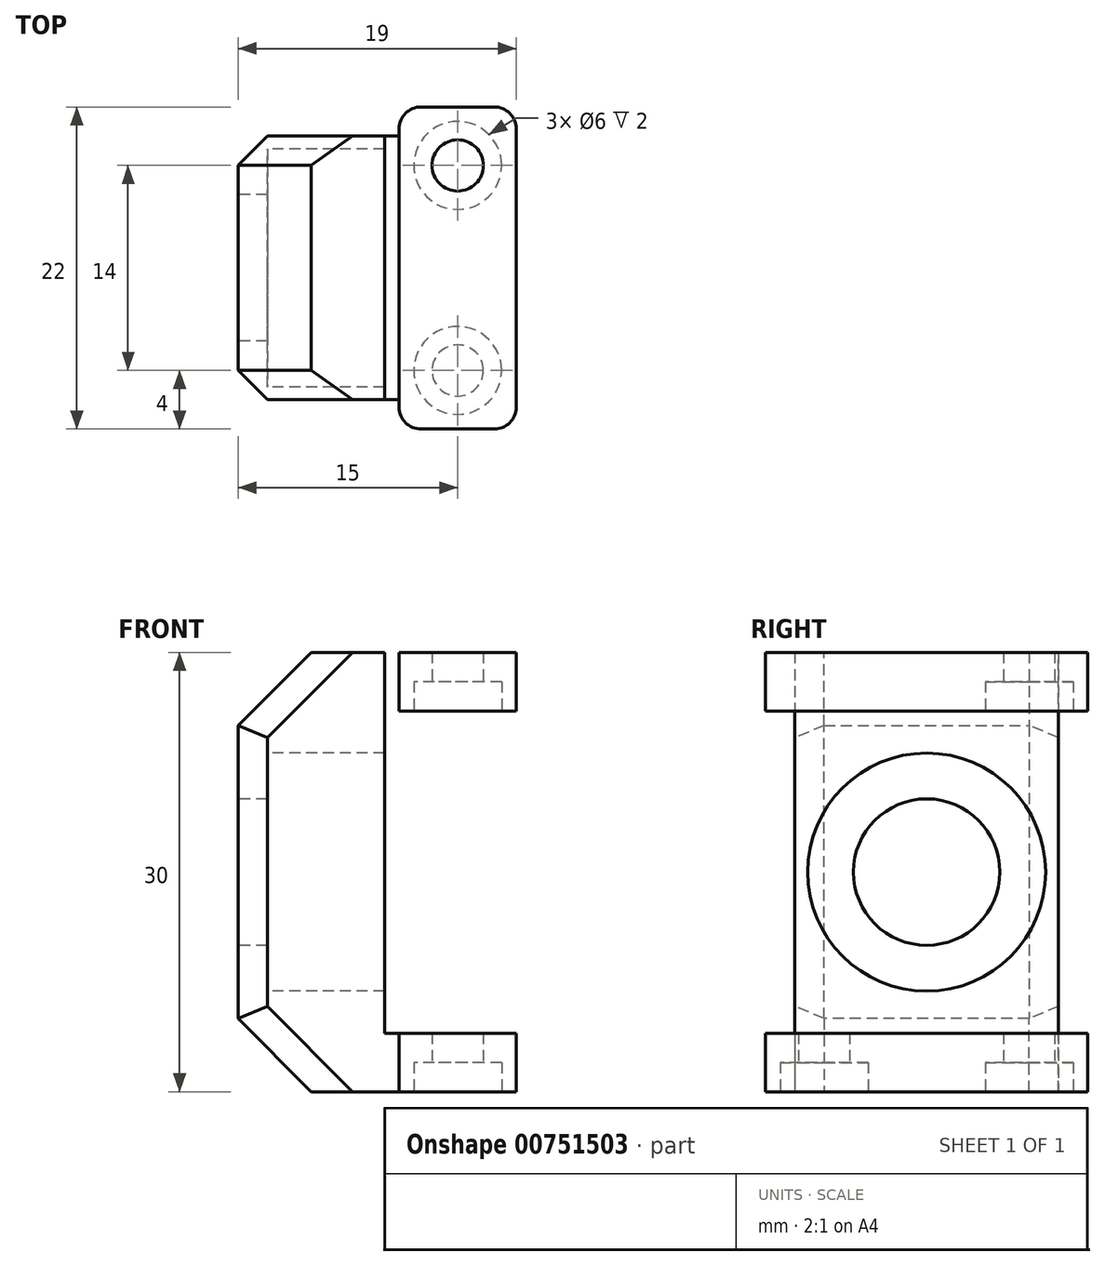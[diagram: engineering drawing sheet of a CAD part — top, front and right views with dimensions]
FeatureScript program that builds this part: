
annotation { "Feature Type Name" : "Feature", "Feature Type Description" : "" }
export const myFeature = defineFeature(function(context is Context, id is Id, definition is map)
    precondition{}
    {
        {
            assignVariable(context, id + "F0", {"name" : "UpperLowerWidth", "anyValue" : 4});
        }
        {
            assignVariable(context, id + "F1", {"name" : "TotalHeight", "anyValue" : 30});
        }
        {
            var Q0;
            Q0=qCreatedBy(makeId("Top.planeOp"),FACE);
            var sketch = newSketch(context, id + "F2", { "sketchPlane" : qUnion([Q0])});
            skLineSegment(sketch, "E0.bottom", {"start": v(-4, 11) * mm, "end": v(4, 11) * mm});
            skLineSegment(sketch, "E0.top", {"start": v(-4, -11) * mm, "end": v(4, -11) * mm});
            skLineSegment(sketch, "E0.left", {"start": v(-4, 11) * mm, "end": v(-4, -11) * mm});
            skLineSegment(sketch, "E0.right", {"start": v(4, 11) * mm, "end": v(4, -11) * mm});
            skPoint(sketch, "E0.middle", {"position": v(0, 0) * mm});
            skCircle(sketch, "E1", {"center": v(0, 7) * mm, "radius": 1.75 * mm});
            skCircle(sketch, "E2", {"center": v(0, -7) * mm, "radius": 1.75 * mm});
            skLineSegment(sketch, "E3.bottom", {"start": v(-4, 9) * mm, "end": v(-15, 9) * mm});
            skLineSegment(sketch, "E3.top", {"start": v(-4, -9) * mm, "end": v(-15, -9) * mm});
            skLineSegment(sketch, "E3.left", {"start": v(-4, 9) * mm, "end": v(-4, -9) * mm});
            skLineSegment(sketch, "E3.right", {"start": v(-15, 9) * mm, "end": v(-15, -9) * mm});
            skLineSegment(sketch, "E4", {"start": v(-4, 9) * mm, "end": v(-4, 11) * mm, "construction": true});
            skLineSegment(sketch, "E5", {"start": v(-4, -9) * mm, "end": v(-4, -11) * mm, "construction": true});
            skLineSegment(sketch, "E6", {"start": v(-5, -9) * mm, "end": v(-5, 9) * mm});
            skCircle(sketch, "E7", {"center": v(0, 7) * mm, "radius": 3 * mm});
            skCircle(sketch, "E8", {"center": v(0, -7) * mm, "radius": 3 * mm});
            skSolve(sketch);
        }
        {
            var Q0;
            {var subQ3=sQuery(id+"F2.wireOp",EDGE,"E0.bottom");Q0=makeQuery(id+"F2.imprint","IMPRINT",FACE,{"disambiguationData":[TD([[makeQuery(id+"F2.imprint","IMPRINT",EDGE,{"derivedFrom":subQ3}),-1.0]])]});}
            var Q1;
            {var subQ1=sQuery(id+"F2.wireOp",EDGE,"E0.top");Q1=makeQuery(id+"F2.imprint","IMPRINT",FACE,{"disambiguationData":[TD([[makeQuery(id+"F2.imprint","IMPRINT",EDGE,{"derivedFrom":subQ1}),1.0]])]});}
            var Q2;
            Q2=makeQuery(id+"F2.imprint","IMPRINT",FACE,{"disambiguationData":[TD([[makeQuery(id+"F2.imprint","IMPRINT",EDGE,{"derivedFrom":sQuery(id+"F2.wireOp",EDGE,"kTuUN5Vh-sZAy-PONC-NSCL-Ygs5GUUw9hLd")}),-1.0]])]});
            var Q3;
            Q3=makeQuery(id+"F2.imprint","IMPRINT",FACE,{"disambiguationData":[TD([[makeQuery(id+"F2.imprint","IMPRINT",EDGE,{"derivedFrom":sQuery(id+"F2.wireOp",EDGE,"kTuUN5Vh-sZAy-PONC-NSCL-Ygs5GUUw9hLd")}),1.0]])]});
            var Q4;
            {var subQ4=sQuery(id+"F2.wireOp",EDGE,"y2zxEj2q-xixG-cvwC-23qs-c7dRdEuyMa0k.left");Q4=makeQuery(id+"F2.imprint","IMPRINT",FACE,{"disambiguationData":[TD([[makeQuery(id+"F2.imprint","IMPRINT",EDGE,{"derivedFrom":subQ4}),-1.0]])]});}
            var Q5;
            {var subQ1=sQuery(id+"F2.wireOp",EDGE,"E3.top");var subQ3=sQuery(id+"F2.wireOp",EDGE,"E6");var subQ4=makeQuery(id+"F2.imprint","INTERSECT",VERTEX,{"derivedFrom":[subQ1,subQ3]});Q5=makeQuery(id+"F2.imprint","IMPRINT",FACE,{"disambiguationData":[TD([[makeQuery(id+"F2.imprint","IMPRINT",EDGE,{"disambiguationData":[TD([[subQ4,1.0]])],"derivedFrom":subQ1}),-1.0]])]});}
            var Q6;
            {var subQ5=sQuery(id+"F2.wireOp",EDGE,"wyvkeBN8-lFPd-MPIe-uRmF-NOTkxEmPuTPF.right");Q6=makeQuery(id+"F2.imprint","IMPRINT",FACE,{"disambiguationData":[TD([[makeQuery(id+"F2.imprint","IMPRINT",EDGE,{"derivedFrom":subQ5}),1.0]])]});}
            var Q7;
            {var subQ1=sQuery(id+"F2.wireOp",EDGE,"E3.bottom");var subQ3=sQuery(id+"F2.wireOp",EDGE,"E6");var subQ4=makeQuery(id+"F2.imprint","INTERSECT",VERTEX,{"derivedFrom":[subQ1,subQ3]});Q7=makeQuery(id+"F2.imprint","IMPRINT",FACE,{"disambiguationData":[TD([[makeQuery(id+"F2.imprint","IMPRINT",EDGE,{"disambiguationData":[TD([[subQ4,1.0]])],"derivedFrom":subQ1}),1.0]])]});}
            extrude(context, id + "F3", {"entities" : qUnion([Q0, Q1, Q2, Q3, Q4, Q5, Q6, Q7]), "depth" : (getVariable(context, 'UpperLowerWidth')) * mm, "offsetDistance" : 25 * mm});
        }
        {
            var Q0;
            Q0=makeQuery(id+"F2.imprint","IMPRINT",FACE,{"disambiguationData":[TD([[makeQuery(id+"F2.imprint","IMPRINT",EDGE,{"derivedFrom":sQuery(id+"F2.wireOp",EDGE,"E2")}),-1.0]])]});
            var Q1;
            {var subQ0=sQuery(id+"F2.wireOp",EDGE,"y2zxEj2q-xixG-cvwC-23qs-c7dRdEuyMa0k.top");var subQ1=sQuery(id+"F2.wireOp",EDGE,"gfawO1WD-zkZ5-YI3A-fLo1-D2l7KtzhZ2Z2");var subQ2=makeQuery(id+"F2.imprint","INTERSECT",VERTEX,{"disambiguationData":[OD(0.0)],"derivedFrom":[subQ1,subQ0]});Q1=makeQuery(id+"F2.imprint","IMPRINT",FACE,{"disambiguationData":[TD([[makeQuery(id+"F2.imprint","IMPRINT",EDGE,{"disambiguationData":[TD([[subQ2,1.0]])],"derivedFrom":subQ1}),1.0]])]});}
            var Q2;
            {var subQ0=sQuery(id+"F2.wireOp",EDGE,"wyvkeBN8-lFPd-MPIe-uRmF-NOTkxEmPuTPF.top");var subQ1=sQuery(id+"F2.wireOp",EDGE,"gfawO1WD-zkZ5-YI3A-fLo1-D2l7KtzhZ2Z2");var subQ2=makeQuery(id+"F2.imprint","INTERSECT",VERTEX,{"disambiguationData":[OD(0.0)],"derivedFrom":[subQ1,subQ0]});Q2=makeQuery(id+"F2.imprint","IMPRINT",FACE,{"disambiguationData":[TD([[makeQuery(id+"F2.imprint","IMPRINT",EDGE,{"disambiguationData":[TD([[subQ2,-1.0]])],"derivedFrom":subQ1}),1.0]])]});}
            var Q3;
            Q3=makeQuery(id+"F2.imprint","IMPRINT",FACE,{"disambiguationData":[TD([[makeQuery(id+"F2.imprint","IMPRINT",EDGE,{"derivedFrom":sQuery(id+"F2.wireOp",EDGE,"E1")}),-1.0]])]});
            extrude(context, id + "F4", {"entities" : qUnion([Q0, Q1, Q2, Q3]), "operationType" : NewBodyOperationType.ADD, "depth" : 4 * mm, "offsetDistance" : 25 * mm, "hasSecondDirection" : true, "secondDirectionOppositeDirection" : false, "secondDirectionDepth" : 2 * mm});
        }
        {
            var Q0;
            {var subQ0=sQuery(id+"F2.wireOp",EDGE,"E3.right");Q0=makeQuery(id+"F2.imprint","IMPRINT",FACE,{"disambiguationData":[TD([[makeQuery(id+"F2.imprint","IMPRINT",EDGE,{"derivedFrom":subQ0}),1.0]])]});}
            extrude(context, id + "F5", {"entities" : qUnion([Q0]), "operationType" : NewBodyOperationType.ADD, "depth" : (getVariable(context, 'TotalHeight')) * mm, "offsetDistance" : 25 * mm});
        }
        {
            var Q0;
            {var subQ0=sQuery(id+"F2.wireOp",EDGE,"UeJNs1Ye-0UtY-b5V1-B9bO-pdQvNy77qKzU");var subQ1=sQuery(id+"F2.wireOp",EDGE,"E2");var subQ2=makeQuery(id+"F2.imprint","INTERSECT",VERTEX,{"disambiguationData":[OD(0.0)],"derivedFrom":[subQ1,subQ0]});Q0=makeQuery(id+"F2.imprint","IMPRINT",FACE,{"disambiguationData":[TD([[makeQuery(id+"F2.imprint","IMPRINT",EDGE,{"disambiguationData":[TD([[subQ2,1.0]])],"derivedFrom":subQ1}),-1.0]])]});}
            var Q1;
            {var subQ1=sQuery(id+"F2.wireOp",EDGE,"E0.bottom");Q1=makeQuery(id+"F2.imprint","IMPRINT",FACE,{"disambiguationData":[TD([[makeQuery(id+"F2.imprint","IMPRINT",EDGE,{"derivedFrom":subQ1}),-1.0]])]});}
            var Q2;
            {var subQ0=sQuery(id+"F2.wireOp",EDGE,"E3.left");Q2=makeQuery(id+"F2.imprint","IMPRINT",FACE,{"disambiguationData":[TD([[makeQuery(id+"F2.imprint","IMPRINT",EDGE,{"derivedFrom":subQ0}),-1.0]])]});}
            var Q3;
            {var subQ0=sQuery(id+"F2.wireOp",EDGE,"UeJNs1Ye-0UtY-b5V1-B9bO-pdQvNy77qKzU");var subQ1=sQuery(id+"F2.wireOp",EDGE,"E2");var subQ2=makeQuery(id+"F2.imprint","INTERSECT",VERTEX,{"disambiguationData":[OD(0.0)],"derivedFrom":[subQ1,subQ0]});Q3=makeQuery(id+"F2.imprint","IMPRINT",FACE,{"disambiguationData":[TD([[makeQuery(id+"F2.imprint","IMPRINT",EDGE,{"disambiguationData":[TD([[subQ2,1.0]])],"derivedFrom":subQ1}),1.0]])]});}
            extrude(context, id + "F6", {"entities" : qUnion([Q0, Q1, Q2, Q3]), "operationType" : NewBodyOperationType.ADD, "depth" : (getVariable(context, 'TotalHeight')) * mm, "offsetDistance" : 25 * mm, "hasSecondDirection" : true, "secondDirectionOppositeDirection" : false, "secondDirectionDepth" : (getVariable(context, 'TotalHeight') - getVariable(context, 'UpperLowerWidth')) * mm});
        }
        {
            var Q0;
            Q0=makeQuery(id+"F5.opExtrude","SWEPT_FACE",FACE,{"disambiguationData":[OSD([sQuery(id+"F2.wireOp",EDGE,"E3.right")])]});
            var sketch = newSketch(context, id + "F7", { "sketchPlane" : qUnion([Q0])});
            skCircle(sketch, "E9", {"center": v(0, 15) * mm, "radius": 8.12 * mm});
            skLineSegment(sketch, "E10", {"start": v(0, 15) * mm, "end": v(0, 4) * mm, "construction": true});
            skCircle(sketch, "E11", {"center": v(0, 15) * mm, "radius": 5 * mm});
            skLineSegment(sketch, "E12", {"start": v(0, 15) * mm, "end": v(0, 26) * mm, "construction": true});
            skSolve(sketch);
        }
        {
            var Q0;
            Q0=makeQuery(id+"F7.imprint","IMPRINT",FACE,{"disambiguationData":[TD([[makeQuery(id+"F7.imprint","IMPRINT",EDGE,{"derivedFrom":sQuery(id+"F7.wireOp",EDGE,"E11")}),1.0]])]});
            var Q1;
            Q1=makeQuery(id+"F7.imprint","IMPRINT",FACE,{"disambiguationData":[TD([[makeQuery(id+"F7.imprint","IMPRINT",EDGE,{"derivedFrom":sQuery(id+"F7.wireOp",EDGE,"E9")}),1.0]])]});
            extrude(context, id + "F8", {"entities" : qUnion([Q0, Q1]), "operationType" : NewBodyOperationType.REMOVE, "oppositeDirection" : true, "depth" : 10 * mm, "offsetDistance" : 25 * mm});
        }
        {
            var Q0;
            Q0=makeQuery(id+"F7.imprint","IMPRINT",FACE,{"disambiguationData":[TD([[makeQuery(id+"F7.imprint","IMPRINT",EDGE,{"derivedFrom":sQuery(id+"F7.wireOp",EDGE,"E9")}),1.0]])]});
            extrude(context, id + "F9", {"entities" : qUnion([Q0]), "operationType" : NewBodyOperationType.ADD, "oppositeDirection" : true, "depth" : 2 * mm, "offsetDistance" : 25 * mm});
        }
        {
            var Q0;
            Q0=makeQuery(id+"F2.imprint","IMPRINT",FACE,{"disambiguationData":[TD([[makeQuery(id+"F2.imprint","IMPRINT",EDGE,{"derivedFrom":sQuery(id+"F2.wireOp",EDGE,"E1")}),-1.0]])]});
            var Q1;
            Q1=makeQuery(id+"F2.imprint","IMPRINT",FACE,{"disambiguationData":[TD([[makeQuery(id+"F2.imprint","IMPRINT",EDGE,{"derivedFrom":sQuery(id+"F2.wireOp",EDGE,"E2")}),-1.0]])]});
            extrude(context, id + "F10", {"entities" : qUnion([Q0, Q1]), "operationType" : NewBodyOperationType.ADD, "depth" : (getVariable(context, 'TotalHeight')) * mm, "offsetDistance" : 25 * mm, "hasSecondDirection" : true, "secondDirectionOppositeDirection" : false, "secondDirectionDepth" : (getVariable(context, 'TotalHeight') - 2) * mm});
        }
        {
            var Q0;
            Q0=makeQuery(id+"F5.opExtrude","CAP_EDGE",EDGE,{"disambiguationData":[OSD([sQuery(id+"F2.wireOp",EDGE,"E3.right")])],"isStart":true});
            var Q1;
            Q1=makeQuery(id+"F5.opExtrude","CAP_EDGE",EDGE,{"disambiguationData":[OSD([sQuery(id+"F2.wireOp",EDGE,"E3.right")])],"isStart":false});
            chamfer(context, id + "F11", {"entities" : qUnion([Q0, Q1]), "width" : 5 * mm, "tangentPropagation" : true});
        }
        {
            var Q0;
            Q0=makeQuery(id+"F5.opExtrude","SWEPT_EDGE",EDGE,{"disambiguationData":[OSD([sQuery(id+"F2.wireOp",EDGE,"E3.top"),sQuery(id+"F2.wireOp",EDGE,"E3.right")])]});
            var Q1;
            Q1=makeQuery(id+"F5.opExtrude","SWEPT_EDGE",EDGE,{"disambiguationData":[OSD([sQuery(id+"F2.wireOp",EDGE,"E3.bottom"),sQuery(id+"F2.wireOp",EDGE,"E3.right")])]});
            var Q2;
            {var subQ0=sQuery(id+"F2.wireOp",EDGE,"E3.bottom");Q2=makeQuery(id+"F11.opChamfer","BLEND_EDGE",EDGE,{"blendedFrom":[makeQuery(id+"F5.opExtrude","CAP_EDGE",EDGE,{"disambiguationData":[OSD([sQuery(id+"F2.wireOp",EDGE,"E3.right")])],"isStart":false}),makeQuery(id+"F6.boolean.opBoolean","MERGE",FACE,{"derivedFrom":[makeQuery(id+"F5.boolean.opBoolean","MERGE",FACE,{"derivedFrom":[makeQuery(id+"F3.opExtrude","SWEPT_FACE",FACE,{"disambiguationData":[OSD([subQ0])]}),makeQuery(id+"F5.opExtrude","SWEPT_FACE",FACE,{"disambiguationData":[OSD([subQ0])]})]}),makeQuery(id+"F6.opExtrude","SWEPT_FACE",FACE,{"disambiguationData":[OSD([subQ0])]})]})],"blendedInto":[makeQuery(id+"F6.boolean.opBoolean","MERGE",FACE,{"derivedFrom":[makeQuery(id+"F5.boolean.opBoolean","MERGE",FACE,{"derivedFrom":[makeQuery(id+"F3.opExtrude","SWEPT_FACE",FACE,{"disambiguationData":[OSD([subQ0])]}),makeQuery(id+"F5.opExtrude","SWEPT_FACE",FACE,{"disambiguationData":[OSD([subQ0])]})]}),makeQuery(id+"F6.opExtrude","SWEPT_FACE",FACE,{"disambiguationData":[OSD([subQ0])]})]})]});}
            var Q3;
            {var subQ0=sQuery(id+"F2.wireOp",EDGE,"E3.top");Q3=makeQuery(id+"F11.opChamfer","BLEND_EDGE",EDGE,{"blendedFrom":[makeQuery(id+"F5.opExtrude","CAP_EDGE",EDGE,{"disambiguationData":[OSD([sQuery(id+"F2.wireOp",EDGE,"E3.right")])],"isStart":false}),makeQuery(id+"F6.boolean.opBoolean","MERGE",FACE,{"derivedFrom":[makeQuery(id+"F5.boolean.opBoolean","MERGE",FACE,{"derivedFrom":[makeQuery(id+"F3.opExtrude","SWEPT_FACE",FACE,{"disambiguationData":[OSD([subQ0])]}),makeQuery(id+"F5.opExtrude","SWEPT_FACE",FACE,{"disambiguationData":[OSD([subQ0])]})]}),makeQuery(id+"F6.opExtrude","SWEPT_FACE",FACE,{"disambiguationData":[OSD([subQ0])]})]})],"blendedInto":[makeQuery(id+"F6.boolean.opBoolean","MERGE",FACE,{"derivedFrom":[makeQuery(id+"F5.boolean.opBoolean","MERGE",FACE,{"derivedFrom":[makeQuery(id+"F3.opExtrude","SWEPT_FACE",FACE,{"disambiguationData":[OSD([subQ0])]}),makeQuery(id+"F5.opExtrude","SWEPT_FACE",FACE,{"disambiguationData":[OSD([subQ0])]})]}),makeQuery(id+"F6.opExtrude","SWEPT_FACE",FACE,{"disambiguationData":[OSD([subQ0])]})]})]});}
            var Q4;
            {var subQ0=sQuery(id+"F2.wireOp",EDGE,"E3.bottom");Q4=makeQuery(id+"F11.opChamfer","BLEND_EDGE",EDGE,{"blendedFrom":[makeQuery(id+"F5.opExtrude","CAP_EDGE",EDGE,{"disambiguationData":[OSD([sQuery(id+"F2.wireOp",EDGE,"E3.right")])],"isStart":true}),makeQuery(id+"F6.boolean.opBoolean","MERGE",FACE,{"derivedFrom":[makeQuery(id+"F5.boolean.opBoolean","MERGE",FACE,{"derivedFrom":[makeQuery(id+"F3.opExtrude","SWEPT_FACE",FACE,{"disambiguationData":[OSD([subQ0])]}),makeQuery(id+"F5.opExtrude","SWEPT_FACE",FACE,{"disambiguationData":[OSD([subQ0])]})]}),makeQuery(id+"F6.opExtrude","SWEPT_FACE",FACE,{"disambiguationData":[OSD([subQ0])]})]})],"blendedInto":[makeQuery(id+"F6.boolean.opBoolean","MERGE",FACE,{"derivedFrom":[makeQuery(id+"F5.boolean.opBoolean","MERGE",FACE,{"derivedFrom":[makeQuery(id+"F3.opExtrude","SWEPT_FACE",FACE,{"disambiguationData":[OSD([subQ0])]}),makeQuery(id+"F5.opExtrude","SWEPT_FACE",FACE,{"disambiguationData":[OSD([subQ0])]})]}),makeQuery(id+"F6.opExtrude","SWEPT_FACE",FACE,{"disambiguationData":[OSD([subQ0])]})]})]});}
            var Q5;
            {var subQ0=sQuery(id+"F2.wireOp",EDGE,"E3.top");Q5=makeQuery(id+"F11.opChamfer","BLEND_EDGE",EDGE,{"blendedFrom":[makeQuery(id+"F5.opExtrude","CAP_EDGE",EDGE,{"disambiguationData":[OSD([sQuery(id+"F2.wireOp",EDGE,"E3.right")])],"isStart":true}),makeQuery(id+"F6.boolean.opBoolean","MERGE",FACE,{"derivedFrom":[makeQuery(id+"F5.boolean.opBoolean","MERGE",FACE,{"derivedFrom":[makeQuery(id+"F3.opExtrude","SWEPT_FACE",FACE,{"disambiguationData":[OSD([subQ0])]}),makeQuery(id+"F5.opExtrude","SWEPT_FACE",FACE,{"disambiguationData":[OSD([subQ0])]})]}),makeQuery(id+"F6.opExtrude","SWEPT_FACE",FACE,{"disambiguationData":[OSD([subQ0])]})]})],"blendedInto":[makeQuery(id+"F6.boolean.opBoolean","MERGE",FACE,{"derivedFrom":[makeQuery(id+"F5.boolean.opBoolean","MERGE",FACE,{"derivedFrom":[makeQuery(id+"F3.opExtrude","SWEPT_FACE",FACE,{"disambiguationData":[OSD([subQ0])]}),makeQuery(id+"F5.opExtrude","SWEPT_FACE",FACE,{"disambiguationData":[OSD([subQ0])]})]}),makeQuery(id+"F6.opExtrude","SWEPT_FACE",FACE,{"disambiguationData":[OSD([subQ0])]})]})]});}
            chamfer(context, id + "F12", {"entities" : qUnion([Q0, Q1, Q2, Q3, Q4, Q5]), "width" : 2 * mm, "tangentPropagation" : true});
        }
        {
            var Q0;
            Q0=makeQuery(id+"F3.opExtrude","SWEPT_EDGE",EDGE,{"disambiguationData":[OSD([sQuery(id+"F2.wireOp",EDGE,"E0.bottom"),sQuery(id+"F2.wireOp",EDGE,"E0.right")])]});
            var Q1;
            Q1=makeQuery(id+"F3.opExtrude","SWEPT_EDGE",EDGE,{"disambiguationData":[OSD([sQuery(id+"F2.wireOp",EDGE,"E0.top"),sQuery(id+"F2.wireOp",EDGE,"E0.right")])]});
            var Q2;
            Q2=makeQuery(id+"F3.opExtrude","SWEPT_EDGE",EDGE,{"disambiguationData":[OSD([sQuery(id+"F2.wireOp",EDGE,"E0.top"),sQuery(id+"F2.wireOp",EDGE,"E0.left")])]});
            var Q3;
            Q3=makeQuery(id+"F3.opExtrude","SWEPT_EDGE",EDGE,{"disambiguationData":[OSD([sQuery(id+"F2.wireOp",EDGE,"E0.bottom"),sQuery(id+"F2.wireOp",EDGE,"E0.left")])]});
            var Q4;
            Q4=makeQuery(id+"F6.opExtrude","SWEPT_EDGE",EDGE,{"disambiguationData":[OSD([sQuery(id+"F2.wireOp",EDGE,"E0.bottom"),sQuery(id+"F2.wireOp",EDGE,"E0.right")])]});
            var Q5;
            Q5=makeQuery(id+"F6.opExtrude","SWEPT_EDGE",EDGE,{"disambiguationData":[OSD([sQuery(id+"F2.wireOp",EDGE,"E0.bottom"),sQuery(id+"F2.wireOp",EDGE,"E0.left")])]});
            var Q6;
            Q6=makeQuery(id+"F6.opExtrude","SWEPT_EDGE",EDGE,{"disambiguationData":[OSD([sQuery(id+"F2.wireOp",EDGE,"E0.top"),sQuery(id+"F2.wireOp",EDGE,"E0.left")])]});
            var Q7;
            Q7=makeQuery(id+"F6.opExtrude","SWEPT_EDGE",EDGE,{"disambiguationData":[OSD([sQuery(id+"F2.wireOp",EDGE,"E0.top"),sQuery(id+"F2.wireOp",EDGE,"E0.right")])]});
            fillet(context, id + "F13", {"entities" : qUnion([Q0, Q1, Q2, Q3, Q4, Q5, Q6, Q7]), "radius" : 1.5 * mm, "tangentPropagation" : true, "allowEdgeOverflow" : false});
        }
    });
